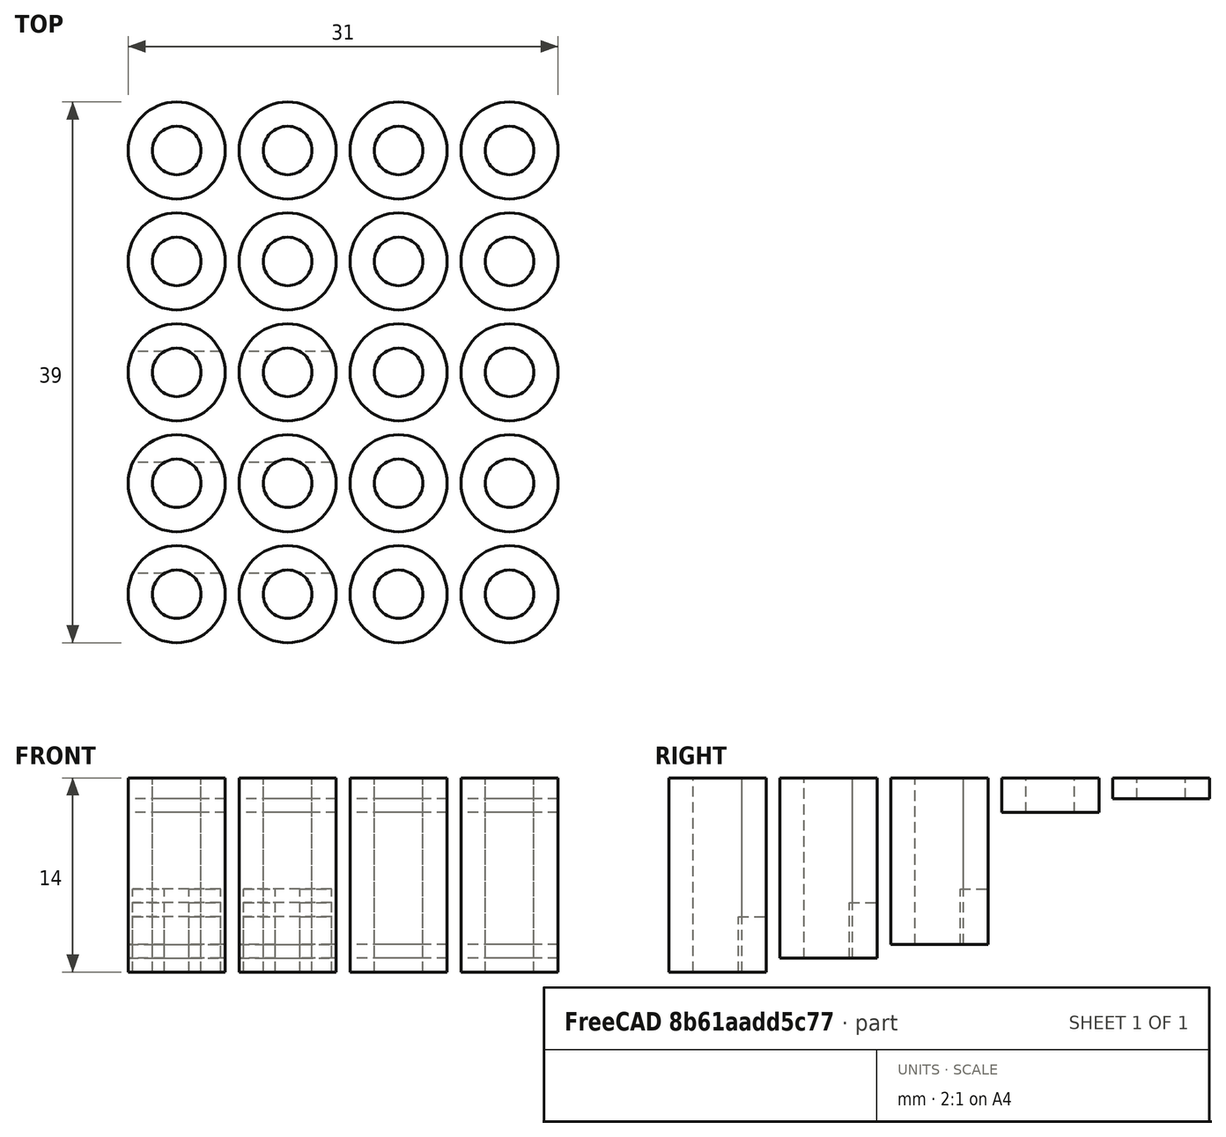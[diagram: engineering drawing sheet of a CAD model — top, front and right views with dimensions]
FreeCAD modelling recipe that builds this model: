
FCSTD DOCUMENT  (FreeCAD 0.16R6707 (Git))
Label: display-spacer
License: All rights reserved
LicenseURL: http://en.wikipedia.org/wiki/All_rights_reserved
objects: Part::Cylinder×38, Part::Cut×26, Part::Box×6
note: 70 computed .brp shape members not serialized (recipe doc carries the construction recipe); baked Part::Feature solids carry a one-line shape summary decoded from their .brp

FEATURE [Part::Cylinder] Cylinder
  Angle = 360
  Height = 20
  Placement = pos=(0,0,-1) rot=(0,0,1;0rad)
  Radius = 1.75
FEATURE [Part::Cylinder] Cylinder001
  Angle = 360
  Height = 13
  Radius = 3.5
FEATURE [Part::Box] Box  label="Cube"
  Height = 5
  Length = 10
  Placement = pos=(-5,1.5,-1) rot=(0,0,1;0rad)
  Width = 10
FEATURE [Part::Cut] Cut
  Base = -> Cylinder001
  Tool = -> Cylinder
FEATURE [Part::Cylinder] Cylinder002
  Angle = 360
  Height = 20
  Placement = pos=(0,0,-1) rot=(0,0,1;0rad)
  Radius = 1.75
FEATURE [Part::Cylinder] Cylinder003
  Angle = 360
  Height = 13
  Radius = 3.5
FEATURE [Part::Cut] Cut001  label="13mm"
  Base = -> Cylinder003
  Placement = pos=(16,-8,0) rot=(0,0,1;0rad)
  Tool = -> Cylinder002
FEATURE [Part::Cut] Cut002  label="13mm-4mm"
  Base = -> Cut
  Placement = pos=(0,-8,0) rot=(0,0,1;0rad)
  Tool = -> Box
FEATURE [Part::Cylinder] Cylinder004
  Angle = 360
  Height = 20
  Placement = pos=(0,0,-1) rot=(0,0,1;0rad)
  Radius = 1.75
FEATURE [Part::Cylinder] Cylinder005
  Angle = 360
  Height = 13
  Radius = 3.5
FEATURE [Part::Box] Box001  label="Cube001"
  Height = 5
  Length = 10
  Placement = pos=(-5,1.5,-1) rot=(0,0,1;0rad)
  Width = 10
FEATURE [Part::Cut] Cut003
  Base = -> Cylinder005
  Tool = -> Cylinder004
FEATURE [Part::Cut] Cut004  label="13mm-4mm001"
  Base = -> Cut003
  Placement = pos=(-8,-8,0) rot=(0,0,1;0rad)
  Tool = -> Box001
FEATURE [Part::Cylinder] Cylinder006
  Angle = 360
  Height = 20
  Placement = pos=(0,0,-1) rot=(0,0,1;0rad)
  Radius = 1.75
FEATURE [Part::Cylinder] Cylinder007
  Angle = 360
  Height = 12
  Radius = 3.5
FEATURE [Part::Box] Box002  label="Cube002"
  Height = 5
  Length = 10
  Placement = pos=(-5,1.5,-1) rot=(0,0,1;0rad)
  Width = 10
FEATURE [Part::Cut] Cut005
  Base = -> Cylinder007
  Tool = -> Cylinder006
FEATURE [Part::Cylinder] Cylinder008
  Angle = 360
  Height = 20
  Placement = pos=(0,0,-1) rot=(0,0,1;0rad)
  Radius = 1.75
FEATURE [Part::Cylinder] Cylinder009
  Angle = 360
  Height = 12
  Placement = pos=(0,0,1) rot=(0,0,1;0rad)
  Radius = 3.5
FEATURE [Part::Cut] Cut006  label="12mm"
  Base = -> Cylinder009
  Placement = pos=(16,0,0) rot=(0,0,1;0rad)
  Tool = -> Cylinder008
FEATURE [Part::Cut] Cut007  label="12mm-4mm"
  Base = -> Cut005
  Placement = pos=(0,0,1) rot=(0,0,1;0rad)
  Tool = -> Box002
FEATURE [Part::Cylinder] Cylinder010
  Angle = 360
  Height = 20
  Placement = pos=(0,0,-1) rot=(0,0,1;0rad)
  Radius = 1.75
FEATURE [Part::Cylinder] Cylinder011
  Angle = 360
  Height = 12
  Radius = 3.5
FEATURE [Part::Box] Box003  label="Cube003"
  Height = 5
  Length = 10
  Placement = pos=(-5,1.5,-1) rot=(0,0,1;0rad)
  Width = 10
FEATURE [Part::Cut] Cut008
  Base = -> Cylinder011
  Tool = -> Cylinder010
FEATURE [Part::Cut] Cut009  label="12mm-4mm001"
  Base = -> Cut008
  Placement = pos=(-8,0,1) rot=(0,0,1;0rad)
  Tool = -> Box003
FEATURE [Part::Cylinder] Cylinder012
  Angle = 360
  Height = 20
  Placement = pos=(0,0,-1) rot=(0,0,1;0rad)
  Radius = 1.75
FEATURE [Part::Cylinder] Cylinder013
  Angle = 360
  Height = 14
  Radius = 3.5
FEATURE [Part::Box] Box004  label="Cube004"
  Height = 5
  Length = 10
  Placement = pos=(-5,1.5,-1) rot=(0,0,1;0rad)
  Width = 10
FEATURE [Part::Cut] Cut010
  Base = -> Cylinder013
  Tool = -> Cylinder012
FEATURE [Part::Cylinder] Cylinder014
  Angle = 360
  Height = 20
  Placement = pos=(0,0,-1) rot=(0,0,1;0rad)
  Radius = 1.75
FEATURE [Part::Cylinder] Cylinder015
  Angle = 360
  Height = 14
  Radius = 3.5
FEATURE [Part::Cut] Cut011  label="14mm"
  Base = -> Cylinder015
  Placement = pos=(16,-16,-1) rot=(0,0,1;0rad)
  Tool = -> Cylinder014
FEATURE [Part::Cut] Cut012  label="14mm-4mm"
  Base = -> Cut010
  Placement = pos=(0,-16,-1) rot=(0,0,1;0rad)
  Tool = -> Box004
FEATURE [Part::Cylinder] Cylinder016
  Angle = 360
  Height = 20
  Placement = pos=(0,0,-1) rot=(0,0,1;0rad)
  Radius = 1.75
FEATURE [Part::Cylinder] Cylinder017
  Angle = 360
  Height = 14
  Radius = 3.5
FEATURE [Part::Box] Box005  label="Cube005"
  Height = 5
  Length = 10
  Placement = pos=(-5,1.5,-1) rot=(0,0,1;0rad)
  Width = 10
FEATURE [Part::Cut] Cut013
  Base = -> Cylinder017
  Tool = -> Cylinder016
FEATURE [Part::Cut] Cut014  label="14mm-4mm001"
  Base = -> Cut013
  Placement = pos=(-8,-16,-1) rot=(0,0,1;0rad)
  Tool = -> Box005
FEATURE [Part::Cylinder] Cylinder018
  Angle = 360
  Height = 20
  Placement = pos=(0,0,-1) rot=(0,0,1;0rad)
  Radius = 1.75
FEATURE [Part::Cylinder] Cylinder019
  Angle = 360
  Height = 2.5
  Placement = pos=(0,0,1) rot=(0,0,1;0rad)
  Radius = 3.5
FEATURE [Part::Cut] Cut015  label="2.5mm"
  Base = -> Cylinder019
  Placement = pos=(16,8,9.5) rot=(0,0,1;0rad)
  Tool = -> Cylinder018
FEATURE [Part::Cylinder] Cylinder020
  Angle = 360
  Height = 20
  Placement = pos=(0,0,-1) rot=(0,0,1;0rad)
  Radius = 1.75
FEATURE [Part::Cylinder] Cylinder021
  Angle = 360
  Height = 1.5
  Placement = pos=(0,0,1) rot=(0,0,1;0rad)
  Radius = 3.5
FEATURE [Part::Cut] Cut016  label="1.5mm"
  Base = -> Cylinder021
  Placement = pos=(16,16,10.5) rot=(0,0,1;0rad)
  Tool = -> Cylinder020
FEATURE [Part::Cylinder] Cylinder022
  Angle = 360
  Height = 20
  Placement = pos=(0,0,-1) rot=(0,0,1;0rad)
  Radius = 1.75
FEATURE [Part::Cylinder] Cylinder023
  Angle = 360
  Height = 2.5
  Placement = pos=(0,0,1) rot=(0,0,1;0rad)
  Radius = 3.5
FEATURE [Part::Cut] Cut017  label="2.5mm001"
  Base = -> Cylinder023
  Placement = pos=(8,8,9.5) rot=(0,0,1;0rad)
  Tool = -> Cylinder022
FEATURE [Part::Cylinder] Cylinder024
  Angle = 360
  Height = 20
  Placement = pos=(0,0,-1) rot=(0,0,1;0rad)
  Radius = 1.75
FEATURE [Part::Cylinder] Cylinder025
  Angle = 360
  Height = 2.5
  Placement = pos=(0,0,1) rot=(0,0,1;0rad)
  Radius = 3.5
FEATURE [Part::Cut] Cut018  label="2.5mm002"
  Base = -> Cylinder025
  Placement = pos=(0,8,9.5) rot=(0,0,1;0rad)
  Tool = -> Cylinder024
FEATURE [Part::Cylinder] Cylinder026
  Angle = 360
  Height = 20
  Placement = pos=(0,0,-1) rot=(0,0,1;0rad)
  Radius = 1.75
FEATURE [Part::Cylinder] Cylinder027
  Angle = 360
  Height = 2.5
  Placement = pos=(0,0,1) rot=(0,0,1;0rad)
  Radius = 3.5
FEATURE [Part::Cut] Cut019  label="2.5mm003"
  Base = -> Cylinder027
  Placement = pos=(-8,8,9.5) rot=(0,0,1;0rad)
  Tool = -> Cylinder026
FEATURE [Part::Cylinder] Cylinder028
  Angle = 360
  Height = 20
  Placement = pos=(0,0,-1) rot=(0,0,1;0rad)
  Radius = 1.75
FEATURE [Part::Cylinder] Cylinder029
  Angle = 360
  Height = 1.5
  Placement = pos=(0,0,1) rot=(0,0,1;0rad)
  Radius = 3.5
FEATURE [Part::Cut] Cut020  label="1.5mm001"
  Base = -> Cylinder029
  Placement = pos=(8,16,10.5) rot=(0,0,1;0rad)
  Tool = -> Cylinder028
FEATURE [Part::Cylinder] Cylinder030
  Angle = 360
  Height = 20
  Placement = pos=(0,0,-1) rot=(0,0,1;0rad)
  Radius = 1.75
FEATURE [Part::Cylinder] Cylinder031
  Angle = 360
  Height = 1.5
  Placement = pos=(0,0,1) rot=(0,0,1;0rad)
  Radius = 3.5
FEATURE [Part::Cut] Cut021  label="1.5mm002"
  Base = -> Cylinder031
  Placement = pos=(0,16,10.5) rot=(0,0,1;0rad)
  Tool = -> Cylinder030
FEATURE [Part::Cylinder] Cylinder032
  Angle = 360
  Height = 20
  Placement = pos=(0,0,-1) rot=(0,0,1;0rad)
  Radius = 1.75
FEATURE [Part::Cylinder] Cylinder033
  Angle = 360
  Height = 1.5
  Placement = pos=(0,0,1) rot=(0,0,1;0rad)
  Radius = 3.5
FEATURE [Part::Cut] Cut022  label="1.5mm003"
  Base = -> Cylinder033
  Placement = pos=(-8,16,10.5) rot=(0,0,1;0rad)
  Tool = -> Cylinder032
FEATURE [Part::Cylinder] Cylinder034
  Angle = 360
  Height = 20
  Placement = pos=(0,0,-1) rot=(0,0,1;0rad)
  Radius = 1.75
FEATURE [Part::Cylinder] Cylinder035
  Angle = 360
  Height = 14
  Radius = 3.5
FEATURE [Part::Cut] Cut023  label="14mm001"
  Base = -> Cylinder035
  Placement = pos=(8,-16,-1) rot=(0,0,1;0rad)
  Tool = -> Cylinder034
FEATURE [Part::Cylinder] Cylinder036
  Angle = 360
  Height = 20
  Placement = pos=(0,0,-1) rot=(0,0,1;0rad)
  Radius = 1.75
FEATURE [Part::Cylinder] Cylinder037
  Angle = 360
  Height = 12
  Placement = pos=(0,0,1) rot=(0,0,1;0rad)
  Radius = 3.5
FEATURE [Part::Cut] Cut024  label="12mm001"
  Base = -> Cylinder037
  Placement = pos=(8,0,0) rot=(0,0,1;0rad)
  Tool = -> Cylinder036
FEATURE [Part::Cut] Cut025  label="13mm001"
  Base = -> Cylinder003
  Placement = pos=(8,-8,0) rot=(0,0,1;0rad)
  Tool = -> Cylinder002
